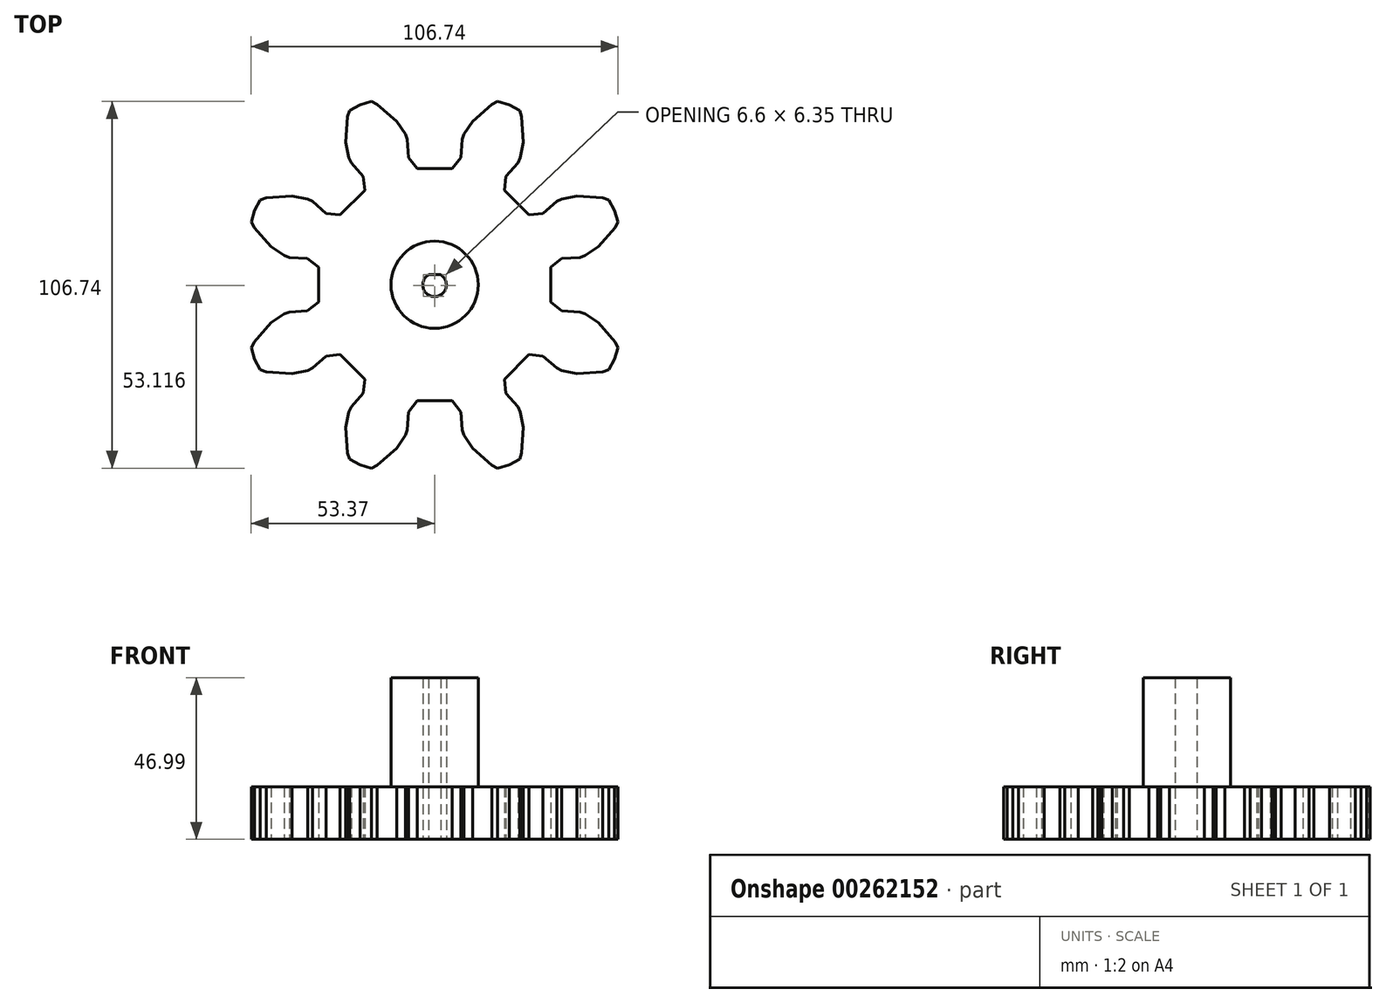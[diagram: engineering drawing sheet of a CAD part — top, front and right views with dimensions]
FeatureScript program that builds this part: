
annotation { "Feature Type Name" : "Feature", "Feature Type Description" : "" }
export const myFeature = defineFeature(function(context is Context, id is Id, definition is map)
    precondition{}
    {
        {
            var Q0;
            Q0=qCreatedBy(makeId("Top.planeOp"),FACE);
            var sketch = newSketch(context, id + "F0", { "sketchPlane" : qUnion([Q0])});
            skLineSegment(sketch, "E0", {"start": v(-50.73, 24.75) * mm, "end": v(-52.36, 21.69) * mm});
            skLineSegment(sketch, "E1", {"start": v(-52.36, 21.69) * mm, "end": v(-53.37, 18.37) * mm});
            skLineSegment(sketch, "E2", {"start": v(-53.37, 18.37) * mm, "end": v(-52.56, 16.72) * mm});
            skLineSegment(sketch, "E3", {"start": v(-52.56, 16.72) * mm, "end": v(-47.6, 11.05) * mm});
            skLineSegment(sketch, "E4", {"start": v(-47.6, 11.05) * mm, "end": v(-43.8, 8.5) * mm});
            skLineSegment(sketch, "E5", {"start": v(-43.8, 8.5) * mm, "end": v(-42.28, 7.97) * mm});
            skLineSegment(sketch, "E6", {"start": v(-42.28, 7.97) * mm, "end": v(-37.01, 7.62) * mm});
            skLineSegment(sketch, "E7", {"start": v(-37.01, 7.62) * mm, "end": v(-33.78, 5.07) * mm});
            skLineSegment(sketch, "E8", {"start": v(-33.78, 5.07) * mm, "end": v(-33.78, -5.07) * mm});
            skLineSegment(sketch, "E9", {"start": v(-33.78, -5.07) * mm, "end": v(-37.01, -7.62) * mm});
            skLineSegment(sketch, "E10", {"start": v(-37.01, -7.62) * mm, "end": v(-42.28, -7.97) * mm});
            skLineSegment(sketch, "E11", {"start": v(-42.28, -7.97) * mm, "end": v(-43.8, -8.5) * mm});
            skLineSegment(sketch, "E12", {"start": v(-43.8, -8.5) * mm, "end": v(-47.6, -11.05) * mm});
            skLineSegment(sketch, "E13", {"start": v(-47.6, -11.05) * mm, "end": v(-52.56, -16.72) * mm});
            skLineSegment(sketch, "E14", {"start": v(-52.56, -16.72) * mm, "end": v(-53.37, -18.37) * mm});
            skLineSegment(sketch, "E15", {"start": v(-53.37, -18.37) * mm, "end": v(-52.36, -21.69) * mm});
            skLineSegment(sketch, "E16", {"start": v(-52.36, -21.69) * mm, "end": v(-50.73, -24.75) * mm});
            skLineSegment(sketch, "E17", {"start": v(-50.73, -24.75) * mm, "end": v(-48.99, -25.34) * mm});
            skLineSegment(sketch, "E18", {"start": v(-48.99, -25.34) * mm, "end": v(-41.47, -25.85) * mm});
            skLineSegment(sketch, "E19", {"start": v(-41.47, -25.85) * mm, "end": v(-36.99, -24.97) * mm});
            skLineSegment(sketch, "E20", {"start": v(-36.99, -24.97) * mm, "end": v(-35.54, -24.26) * mm});
            skLineSegment(sketch, "E21", {"start": v(-35.54, -24.26) * mm, "end": v(-31.56, -20.79) * mm});
            skLineSegment(sketch, "E22", {"start": v(-31.56, -20.79) * mm, "end": v(-27.47, -20.3) * mm});
            skLineSegment(sketch, "E23", {"start": v(-27.47, -20.3) * mm, "end": v(-20.3, -27.47) * mm});
            skLineSegment(sketch, "E24", {"start": v(-20.3, -27.47) * mm, "end": v(-20.79, -31.56) * mm});
            skLineSegment(sketch, "E25", {"start": v(-20.79, -31.56) * mm, "end": v(-24.26, -35.54) * mm});
            skLineSegment(sketch, "E26", {"start": v(-24.26, -35.54) * mm, "end": v(-24.97, -36.99) * mm});
            skLineSegment(sketch, "E27", {"start": v(-24.97, -36.99) * mm, "end": v(-25.85, -41.47) * mm});
            skLineSegment(sketch, "E28", {"start": v(-25.85, -41.47) * mm, "end": v(-25.34, -48.99) * mm});
            skLineSegment(sketch, "E29", {"start": v(-25.34, -48.99) * mm, "end": v(-24.75, -50.73) * mm});
            skLineSegment(sketch, "E30", {"start": v(-24.75, -50.73) * mm, "end": v(-21.69, -52.36) * mm});
            skLineSegment(sketch, "E31", {"start": v(-21.69, -52.36) * mm, "end": v(-18.37, -53.37) * mm});
            skLineSegment(sketch, "E32", {"start": v(-18.37, -53.37) * mm, "end": v(-16.72, -52.56) * mm});
            skLineSegment(sketch, "E33", {"start": v(-16.72, -52.56) * mm, "end": v(-11.05, -47.6) * mm});
            skLineSegment(sketch, "E34", {"start": v(-11.05, -47.6) * mm, "end": v(-8.5, -43.8) * mm});
            skLineSegment(sketch, "E35", {"start": v(-8.5, -43.8) * mm, "end": v(-7.97, -42.28) * mm});
            skLineSegment(sketch, "E36", {"start": v(-7.97, -42.28) * mm, "end": v(-7.62, -37.01) * mm});
            skLineSegment(sketch, "E37", {"start": v(-7.62, -37.01) * mm, "end": v(-5.07, -33.78) * mm});
            skLineSegment(sketch, "E38", {"start": v(-5.07, -33.78) * mm, "end": v(5.07, -33.78) * mm});
            skLineSegment(sketch, "E39", {"start": v(5.07, -33.78) * mm, "end": v(7.62, -37.01) * mm});
            skLineSegment(sketch, "E40", {"start": v(7.62, -37.01) * mm, "end": v(7.97, -42.28) * mm});
            skLineSegment(sketch, "E41", {"start": v(7.97, -42.28) * mm, "end": v(8.5, -43.8) * mm});
            skLineSegment(sketch, "E42", {"start": v(8.5, -43.8) * mm, "end": v(11.05, -47.6) * mm});
            skLineSegment(sketch, "E43", {"start": v(11.05, -47.6) * mm, "end": v(16.72, -52.56) * mm});
            skLineSegment(sketch, "E44", {"start": v(16.72, -52.56) * mm, "end": v(18.37, -53.37) * mm});
            skLineSegment(sketch, "E45", {"start": v(18.37, -53.37) * mm, "end": v(21.69, -52.36) * mm});
            skLineSegment(sketch, "E46", {"start": v(21.69, -52.36) * mm, "end": v(24.75, -50.73) * mm});
            skLineSegment(sketch, "E47", {"start": v(24.75, -50.73) * mm, "end": v(25.34, -48.99) * mm});
            skLineSegment(sketch, "E48", {"start": v(25.34, -48.99) * mm, "end": v(25.85, -41.47) * mm});
            skLineSegment(sketch, "E49", {"start": v(25.85, -41.47) * mm, "end": v(24.97, -36.99) * mm});
            skLineSegment(sketch, "E50", {"start": v(24.97, -36.99) * mm, "end": v(24.26, -35.54) * mm});
            skLineSegment(sketch, "E51", {"start": v(24.26, -35.54) * mm, "end": v(20.79, -31.56) * mm});
            skLineSegment(sketch, "E52", {"start": v(20.79, -31.56) * mm, "end": v(20.3, -27.47) * mm});
            skLineSegment(sketch, "E53", {"start": v(20.3, -27.47) * mm, "end": v(27.47, -20.3) * mm});
            skLineSegment(sketch, "E54", {"start": v(27.47, -20.3) * mm, "end": v(31.56, -20.79) * mm});
            skLineSegment(sketch, "E55", {"start": v(31.56, -20.79) * mm, "end": v(35.54, -24.26) * mm});
            skLineSegment(sketch, "E56", {"start": v(35.54, -24.26) * mm, "end": v(36.99, -24.97) * mm});
            skLineSegment(sketch, "E57", {"start": v(36.99, -24.97) * mm, "end": v(41.47, -25.85) * mm});
            skLineSegment(sketch, "E58", {"start": v(41.47, -25.85) * mm, "end": v(48.99, -25.34) * mm});
            skLineSegment(sketch, "E59", {"start": v(48.99, -25.34) * mm, "end": v(50.73, -24.75) * mm});
            skLineSegment(sketch, "E60", {"start": v(50.73, -24.75) * mm, "end": v(52.36, -21.69) * mm});
            skLineSegment(sketch, "E61", {"start": v(52.36, -21.69) * mm, "end": v(53.37, -18.37) * mm});
            skLineSegment(sketch, "E62", {"start": v(53.37, -18.37) * mm, "end": v(52.56, -16.72) * mm});
            skLineSegment(sketch, "E63", {"start": v(52.56, -16.72) * mm, "end": v(47.6, -11.05) * mm});
            skLineSegment(sketch, "E64", {"start": v(47.6, -11.05) * mm, "end": v(43.8, -8.5) * mm});
            skLineSegment(sketch, "E65", {"start": v(43.8, -8.5) * mm, "end": v(42.28, -7.97) * mm});
            skLineSegment(sketch, "E66", {"start": v(42.28, -7.97) * mm, "end": v(37.01, -7.62) * mm});
            skLineSegment(sketch, "E67", {"start": v(37.01, -7.62) * mm, "end": v(33.78, -5.07) * mm});
            skLineSegment(sketch, "E68", {"start": v(33.78, -5.07) * mm, "end": v(33.78, 5.07) * mm});
            skLineSegment(sketch, "E69", {"start": v(33.78, 5.07) * mm, "end": v(37.01, 7.62) * mm});
            skLineSegment(sketch, "E70", {"start": v(37.01, 7.62) * mm, "end": v(42.28, 7.97) * mm});
            skLineSegment(sketch, "E71", {"start": v(42.28, 7.97) * mm, "end": v(43.8, 8.5) * mm});
            skLineSegment(sketch, "E72", {"start": v(43.8, 8.5) * mm, "end": v(47.6, 11.05) * mm});
            skLineSegment(sketch, "E73", {"start": v(47.6, 11.05) * mm, "end": v(52.56, 16.72) * mm});
            skLineSegment(sketch, "E74", {"start": v(52.56, 16.72) * mm, "end": v(53.37, 18.37) * mm});
            skLineSegment(sketch, "E75", {"start": v(53.37, 18.37) * mm, "end": v(52.36, 21.69) * mm});
            skLineSegment(sketch, "E76", {"start": v(52.36, 21.69) * mm, "end": v(50.73, 24.75) * mm});
            skLineSegment(sketch, "E77", {"start": v(50.73, 24.75) * mm, "end": v(48.99, 25.34) * mm});
            skLineSegment(sketch, "E78", {"start": v(48.99, 25.34) * mm, "end": v(41.47, 25.85) * mm});
            skLineSegment(sketch, "E79", {"start": v(41.47, 25.85) * mm, "end": v(36.99, 24.97) * mm});
            skLineSegment(sketch, "E80", {"start": v(36.99, 24.97) * mm, "end": v(35.54, 24.26) * mm});
            skLineSegment(sketch, "E81", {"start": v(35.54, 24.26) * mm, "end": v(31.56, 20.79) * mm});
            skLineSegment(sketch, "E82", {"start": v(31.56, 20.79) * mm, "end": v(27.47, 20.3) * mm});
            skLineSegment(sketch, "E83", {"start": v(27.47, 20.3) * mm, "end": v(20.3, 27.47) * mm});
            skLineSegment(sketch, "E84", {"start": v(20.3, 27.47) * mm, "end": v(20.79, 31.56) * mm});
            skLineSegment(sketch, "E85", {"start": v(20.79, 31.56) * mm, "end": v(24.26, 35.54) * mm});
            skLineSegment(sketch, "E86", {"start": v(24.26, 35.54) * mm, "end": v(24.97, 36.99) * mm});
            skLineSegment(sketch, "E87", {"start": v(24.97, 36.99) * mm, "end": v(25.85, 41.47) * mm});
            skLineSegment(sketch, "E88", {"start": v(25.85, 41.47) * mm, "end": v(25.34, 48.99) * mm});
            skLineSegment(sketch, "E89", {"start": v(25.34, 48.99) * mm, "end": v(24.75, 50.73) * mm});
            skLineSegment(sketch, "E90", {"start": v(24.75, 50.73) * mm, "end": v(21.69, 52.36) * mm});
            skLineSegment(sketch, "E91", {"start": v(21.69, 52.36) * mm, "end": v(18.37, 53.37) * mm});
            skLineSegment(sketch, "E92", {"start": v(18.37, 53.37) * mm, "end": v(16.72, 52.56) * mm});
            skLineSegment(sketch, "E93", {"start": v(16.72, 52.56) * mm, "end": v(11.05, 47.6) * mm});
            skLineSegment(sketch, "E94", {"start": v(11.05, 47.6) * mm, "end": v(8.5, 43.8) * mm});
            skLineSegment(sketch, "E95", {"start": v(8.5, 43.8) * mm, "end": v(7.97, 42.28) * mm});
            skLineSegment(sketch, "E96", {"start": v(7.97, 42.28) * mm, "end": v(7.62, 37.01) * mm});
            skLineSegment(sketch, "E97", {"start": v(7.62, 37.01) * mm, "end": v(5.07, 33.78) * mm});
            skLineSegment(sketch, "E98", {"start": v(5.07, 33.78) * mm, "end": v(-5.07, 33.78) * mm});
            skLineSegment(sketch, "E99", {"start": v(-5.07, 33.78) * mm, "end": v(-7.62, 37.01) * mm});
            skLineSegment(sketch, "E100", {"start": v(-7.62, 37.01) * mm, "end": v(-7.97, 42.28) * mm});
            skLineSegment(sketch, "E101", {"start": v(-7.97, 42.28) * mm, "end": v(-8.5, 43.8) * mm});
            skLineSegment(sketch, "E102", {"start": v(-8.5, 43.8) * mm, "end": v(-11.05, 47.6) * mm});
            skLineSegment(sketch, "E103", {"start": v(-11.05, 47.6) * mm, "end": v(-16.72, 52.56) * mm});
            skLineSegment(sketch, "E104", {"start": v(-16.72, 52.56) * mm, "end": v(-18.37, 53.37) * mm});
            skLineSegment(sketch, "E105", {"start": v(-18.37, 53.37) * mm, "end": v(-21.69, 52.36) * mm});
            skLineSegment(sketch, "E106", {"start": v(-21.69, 52.36) * mm, "end": v(-24.75, 50.73) * mm});
            skLineSegment(sketch, "E107", {"start": v(-24.75, 50.73) * mm, "end": v(-25.34, 48.99) * mm});
            skLineSegment(sketch, "E108", {"start": v(-25.34, 48.99) * mm, "end": v(-25.85, 41.47) * mm});
            skLineSegment(sketch, "E109", {"start": v(-25.85, 41.47) * mm, "end": v(-24.97, 36.99) * mm});
            skLineSegment(sketch, "E110", {"start": v(-24.97, 36.99) * mm, "end": v(-24.26, 35.54) * mm});
            skLineSegment(sketch, "E111", {"start": v(-24.26, 35.54) * mm, "end": v(-20.79, 31.56) * mm});
            skLineSegment(sketch, "E112", {"start": v(-20.79, 31.56) * mm, "end": v(-20.3, 27.47) * mm});
            skLineSegment(sketch, "E113", {"start": v(-20.3, 27.47) * mm, "end": v(-27.47, 20.3) * mm});
            skLineSegment(sketch, "E114", {"start": v(-27.47, 20.3) * mm, "end": v(-31.56, 20.79) * mm});
            skLineSegment(sketch, "E115", {"start": v(-31.56, 20.79) * mm, "end": v(-35.54, 24.26) * mm});
            skLineSegment(sketch, "E116", {"start": v(-35.54, 24.26) * mm, "end": v(-36.99, 24.97) * mm});
            skLineSegment(sketch, "E117", {"start": v(-36.99, 24.97) * mm, "end": v(-41.47, 25.85) * mm});
            skLineSegment(sketch, "E118", {"start": v(-41.47, 25.85) * mm, "end": v(-48.99, 25.34) * mm});
            skLineSegment(sketch, "E119", {"start": v(-48.99, 25.34) * mm, "end": v(-50.73, 24.75) * mm});
            skLineSegment(sketch, "E120", {"start": v(-5.04, 7.34) * mm, "end": v(-3.4, 8.22) * mm});
            skLineSegment(sketch, "E121", {"start": v(-3.4, 8.22) * mm, "end": v(-1.62, 8.75) * mm});
            skLineSegment(sketch, "E122", {"start": v(-1.62, 8.75) * mm, "end": v(0.23, 8.9) * mm});
            skLineSegment(sketch, "E123", {"start": v(0.23, 8.9) * mm, "end": v(2.08, 8.66) * mm});
            skLineSegment(sketch, "E124", {"start": v(2.08, 8.66) * mm, "end": v(3.83, 8.04) * mm});
            skLineSegment(sketch, "E125", {"start": v(3.83, 8.04) * mm, "end": v(5.42, 7.06) * mm});
            skLineSegment(sketch, "E126", {"start": v(5.42, 7.06) * mm, "end": v(6.77, 5.78) * mm});
            skLineSegment(sketch, "E127", {"start": v(6.77, 5.78) * mm, "end": v(7.82, 4.25) * mm});
            skLineSegment(sketch, "E128", {"start": v(7.82, 4.25) * mm, "end": v(8.54, 2.53) * mm});
            skLineSegment(sketch, "E129", {"start": v(8.54, 2.53) * mm, "end": v(8.87, 0.7) * mm});
            skLineSegment(sketch, "E130", {"start": v(8.87, 0.7) * mm, "end": v(8.83, -1.16) * mm});
            skLineSegment(sketch, "E131", {"start": v(8.83, -1.16) * mm, "end": v(8.4, -2.97) * mm});
            skLineSegment(sketch, "E132", {"start": v(8.4, -2.97) * mm, "end": v(7.6, -4.65) * mm});
            skLineSegment(sketch, "E133", {"start": v(7.6, -4.65) * mm, "end": v(6.46, -6.13) * mm});
            skLineSegment(sketch, "E134", {"start": v(6.46, -6.13) * mm, "end": v(5.04, -7.34) * mm});
            skLineSegment(sketch, "E135", {"start": v(5.04, -7.34) * mm, "end": v(3.4, -8.22) * mm});
            skLineSegment(sketch, "E136", {"start": v(3.4, -8.22) * mm, "end": v(1.62, -8.75) * mm});
            skLineSegment(sketch, "E137", {"start": v(1.62, -8.75) * mm, "end": v(-0.23, -8.9) * mm});
            skLineSegment(sketch, "E138", {"start": v(-0.23, -8.9) * mm, "end": v(-2.08, -8.66) * mm});
            skLineSegment(sketch, "E139", {"start": v(-2.08, -8.66) * mm, "end": v(-3.83, -8.04) * mm});
            skLineSegment(sketch, "E140", {"start": v(-3.83, -8.04) * mm, "end": v(-5.42, -7.06) * mm});
            skLineSegment(sketch, "E141", {"start": v(-5.42, -7.06) * mm, "end": v(-6.77, -5.78) * mm});
            skLineSegment(sketch, "E142", {"start": v(-6.77, -5.78) * mm, "end": v(-7.82, -4.25) * mm});
            skLineSegment(sketch, "E143", {"start": v(-7.82, -4.25) * mm, "end": v(-8.54, -2.53) * mm});
            skLineSegment(sketch, "E144", {"start": v(-8.54, -2.53) * mm, "end": v(-8.87, -0.7) * mm});
            skLineSegment(sketch, "E145", {"start": v(-8.87, -0.7) * mm, "end": v(-8.83, 1.16) * mm});
            skLineSegment(sketch, "E146", {"start": v(-8.83, 1.16) * mm, "end": v(-8.4, 2.97) * mm});
            skLineSegment(sketch, "E147", {"start": v(-8.4, 2.97) * mm, "end": v(-7.6, 4.65) * mm});
            skLineSegment(sketch, "E148", {"start": v(-7.6, 4.65) * mm, "end": v(-6.46, 6.13) * mm});
            skLineSegment(sketch, "E149", {"start": v(-6.46, 6.13) * mm, "end": v(-5.04, 7.34) * mm});
            skSolve(sketch);
        }
        {
            var Q0;
            Q0=makeQuery(id+"F0.imprint","IMPRINT",FACE,{"disambiguationData":[TD([[makeQuery(id+"F0.imprint","IMPRINT",EDGE,{"derivedFrom":sQuery(id+"F0.wireOp",EDGE,"E0")}),1.0]])]});
            var Q1;
            Q1=makeQuery(id+"F0.imprint","IMPRINT",FACE,{"disambiguationData":[TD([[makeQuery(id+"F0.imprint","IMPRINT",EDGE,{"derivedFrom":sQuery(id+"F0.wireOp",EDGE,"E120")}),-1.0]])]});
            extrude(context, id + "F1", {"entities" : qUnion([Q0, Q1]), "depth" : 15.24 * mm});
        }
        {
            var Q0;
            Q0=makeQuery(id+"F1.opExtrude","CAP_FACE",FACE,{"disambiguationData":[OSD([sQuery(id+"F0.wireOp",EDGE,"E0"),sQuery(id+"F0.wireOp",EDGE,"E1"),sQuery(id+"F0.wireOp",EDGE,"E2"),sQuery(id+"F0.wireOp",EDGE,"E3"),sQuery(id+"F0.wireOp",EDGE,"E4"),sQuery(id+"F0.wireOp",EDGE,"E5"),sQuery(id+"F0.wireOp",EDGE,"E6"),sQuery(id+"F0.wireOp",EDGE,"E7"),sQuery(id+"F0.wireOp",EDGE,"E8"),sQuery(id+"F0.wireOp",EDGE,"E9"),sQuery(id+"F0.wireOp",EDGE,"E10"),sQuery(id+"F0.wireOp",EDGE,"E11"),sQuery(id+"F0.wireOp",EDGE,"E12"),sQuery(id+"F0.wireOp",EDGE,"E13"),sQuery(id+"F0.wireOp",EDGE,"E14"),sQuery(id+"F0.wireOp",EDGE,"E15"),sQuery(id+"F0.wireOp",EDGE,"E16"),sQuery(id+"F0.wireOp",EDGE,"E17"),sQuery(id+"F0.wireOp",EDGE,"E18"),sQuery(id+"F0.wireOp",EDGE,"E19"),sQuery(id+"F0.wireOp",EDGE,"E20"),sQuery(id+"F0.wireOp",EDGE,"E21"),sQuery(id+"F0.wireOp",EDGE,"E22"),sQuery(id+"F0.wireOp",EDGE,"E23"),sQuery(id+"F0.wireOp",EDGE,"E24"),sQuery(id+"F0.wireOp",EDGE,"E25"),sQuery(id+"F0.wireOp",EDGE,"E26"),sQuery(id+"F0.wireOp",EDGE,"E27"),sQuery(id+"F0.wireOp",EDGE,"E28"),sQuery(id+"F0.wireOp",EDGE,"E29"),sQuery(id+"F0.wireOp",EDGE,"E30"),sQuery(id+"F0.wireOp",EDGE,"E31"),sQuery(id+"F0.wireOp",EDGE,"E32"),sQuery(id+"F0.wireOp",EDGE,"E33"),sQuery(id+"F0.wireOp",EDGE,"E34"),sQuery(id+"F0.wireOp",EDGE,"E35"),sQuery(id+"F0.wireOp",EDGE,"E36"),sQuery(id+"F0.wireOp",EDGE,"E37"),sQuery(id+"F0.wireOp",EDGE,"E38"),sQuery(id+"F0.wireOp",EDGE,"E39"),sQuery(id+"F0.wireOp",EDGE,"E40"),sQuery(id+"F0.wireOp",EDGE,"E41"),sQuery(id+"F0.wireOp",EDGE,"E42"),sQuery(id+"F0.wireOp",EDGE,"E43"),sQuery(id+"F0.wireOp",EDGE,"E44"),sQuery(id+"F0.wireOp",EDGE,"E45"),sQuery(id+"F0.wireOp",EDGE,"E46"),sQuery(id+"F0.wireOp",EDGE,"E47"),sQuery(id+"F0.wireOp",EDGE,"E48"),sQuery(id+"F0.wireOp",EDGE,"E49"),sQuery(id+"F0.wireOp",EDGE,"E50"),sQuery(id+"F0.wireOp",EDGE,"E51"),sQuery(id+"F0.wireOp",EDGE,"E52"),sQuery(id+"F0.wireOp",EDGE,"E53"),sQuery(id+"F0.wireOp",EDGE,"E54"),sQuery(id+"F0.wireOp",EDGE,"E55"),sQuery(id+"F0.wireOp",EDGE,"E56"),sQuery(id+"F0.wireOp",EDGE,"E57"),sQuery(id+"F0.wireOp",EDGE,"E58"),sQuery(id+"F0.wireOp",EDGE,"E59"),sQuery(id+"F0.wireOp",EDGE,"E60"),sQuery(id+"F0.wireOp",EDGE,"E61"),sQuery(id+"F0.wireOp",EDGE,"E62"),sQuery(id+"F0.wireOp",EDGE,"E63"),sQuery(id+"F0.wireOp",EDGE,"E64"),sQuery(id+"F0.wireOp",EDGE,"E65"),sQuery(id+"F0.wireOp",EDGE,"E66"),sQuery(id+"F0.wireOp",EDGE,"E67"),sQuery(id+"F0.wireOp",EDGE,"E68"),sQuery(id+"F0.wireOp",EDGE,"E69"),sQuery(id+"F0.wireOp",EDGE,"E70"),sQuery(id+"F0.wireOp",EDGE,"E71"),sQuery(id+"F0.wireOp",EDGE,"E72"),sQuery(id+"F0.wireOp",EDGE,"E73"),sQuery(id+"F0.wireOp",EDGE,"E74"),sQuery(id+"F0.wireOp",EDGE,"E75"),sQuery(id+"F0.wireOp",EDGE,"E76"),sQuery(id+"F0.wireOp",EDGE,"E77"),sQuery(id+"F0.wireOp",EDGE,"E78"),sQuery(id+"F0.wireOp",EDGE,"E79"),sQuery(id+"F0.wireOp",EDGE,"E80"),sQuery(id+"F0.wireOp",EDGE,"E81"),sQuery(id+"F0.wireOp",EDGE,"E82"),sQuery(id+"F0.wireOp",EDGE,"E83"),sQuery(id+"F0.wireOp",EDGE,"E84"),sQuery(id+"F0.wireOp",EDGE,"E85"),sQuery(id+"F0.wireOp",EDGE,"E86"),sQuery(id+"F0.wireOp",EDGE,"E87"),sQuery(id+"F0.wireOp",EDGE,"E88"),sQuery(id+"F0.wireOp",EDGE,"E89"),sQuery(id+"F0.wireOp",EDGE,"E90"),sQuery(id+"F0.wireOp",EDGE,"E91"),sQuery(id+"F0.wireOp",EDGE,"E92"),sQuery(id+"F0.wireOp",EDGE,"E93"),sQuery(id+"F0.wireOp",EDGE,"E94"),sQuery(id+"F0.wireOp",EDGE,"E95"),sQuery(id+"F0.wireOp",EDGE,"E96"),sQuery(id+"F0.wireOp",EDGE,"E97"),sQuery(id+"F0.wireOp",EDGE,"E98"),sQuery(id+"F0.wireOp",EDGE,"E99"),sQuery(id+"F0.wireOp",EDGE,"E100"),sQuery(id+"F0.wireOp",EDGE,"E101"),sQuery(id+"F0.wireOp",EDGE,"E102"),sQuery(id+"F0.wireOp",EDGE,"E103"),sQuery(id+"F0.wireOp",EDGE,"E104"),sQuery(id+"F0.wireOp",EDGE,"E105"),sQuery(id+"F0.wireOp",EDGE,"E106"),sQuery(id+"F0.wireOp",EDGE,"E107"),sQuery(id+"F0.wireOp",EDGE,"E108"),sQuery(id+"F0.wireOp",EDGE,"E109"),sQuery(id+"F0.wireOp",EDGE,"E110"),sQuery(id+"F0.wireOp",EDGE,"E111"),sQuery(id+"F0.wireOp",EDGE,"E112"),sQuery(id+"F0.wireOp",EDGE,"E113"),sQuery(id+"F0.wireOp",EDGE,"E114"),sQuery(id+"F0.wireOp",EDGE,"E115"),sQuery(id+"F0.wireOp",EDGE,"E116"),sQuery(id+"F0.wireOp",EDGE,"E117"),sQuery(id+"F0.wireOp",EDGE,"E118"),sQuery(id+"F0.wireOp",EDGE,"E119")])],"isStart":false});
            var sketch = newSketch(context, id + "F2", { "sketchPlane" : qUnion([Q0])});
            skCircle(sketch, "E150", {"center": v(0, 0) * mm, "radius": 3.43 * mm});
            skLineSegment(sketch, "E151", {"start": v(4.59, 2.92) * mm, "end": v(-4.97, 2.92) * mm});
            skCircle(sketch, "E152", {"center": v(0, 0) * mm, "radius": 12.7 * mm});
            skCircle(sketch, "E153", {"center": v(0, 0) * mm, "radius": 19.05 * mm});
            skSolve(sketch);
        }
        {
            var Q0;
            Q0=makeQuery(id+"F2.imprint","IMPRINT",FACE,{"disambiguationData":[TD([[makeQuery(id+"F2.imprint","IMPRINT",EDGE,{"derivedFrom":sQuery(id+"F2.wireOp",EDGE,"E152")}),1.0]])]});
            var Q1;
            {var subQ0=sQuery(id+"F2.wireOp",EDGE,"E151");var subQ1=sQuery(id+"F2.wireOp",EDGE,"E150");var subQ2=makeQuery(id+"F2.imprint","INTERSECT",VERTEX,{"disambiguationData":[OD(0.0)],"derivedFrom":[subQ1,subQ0]});Q1=makeQuery(id+"F2.imprint","IMPRINT",FACE,{"disambiguationData":[TD([[makeQuery(id+"F2.imprint","IMPRINT",EDGE,{"disambiguationData":[TD([[subQ2,1.0]])],"derivedFrom":subQ1}),1.0]])]});}
            extrude(context, id + "F3", {"entities" : qUnion([Q0, Q1]), "operationType" : NewBodyOperationType.ADD, "depth" : 31.75 * mm});
        }
        {
            var Q0;
            Q0=makeQuery(id+"F3.boolean.opBoolean","SPLIT",FACE,{"disambiguationData":[TD([makeQuery(id+"F3.opExtrude","SWEPT_FACE",FACE,{"disambiguationData":[OSD([sQuery(id+"F2.wireOp",EDGE,"E150")])]})])],"derivedFrom":makeQuery(id+"F1.opExtrude","CAP_FACE",FACE,{"disambiguationData":[OSD([sQuery(id+"F0.wireOp",EDGE,"E0"),sQuery(id+"F0.wireOp",EDGE,"E1"),sQuery(id+"F0.wireOp",EDGE,"E2"),sQuery(id+"F0.wireOp",EDGE,"E3"),sQuery(id+"F0.wireOp",EDGE,"E4"),sQuery(id+"F0.wireOp",EDGE,"E5"),sQuery(id+"F0.wireOp",EDGE,"E6"),sQuery(id+"F0.wireOp",EDGE,"E7"),sQuery(id+"F0.wireOp",EDGE,"E8"),sQuery(id+"F0.wireOp",EDGE,"E9"),sQuery(id+"F0.wireOp",EDGE,"E10"),sQuery(id+"F0.wireOp",EDGE,"E11"),sQuery(id+"F0.wireOp",EDGE,"E12"),sQuery(id+"F0.wireOp",EDGE,"E13"),sQuery(id+"F0.wireOp",EDGE,"E14"),sQuery(id+"F0.wireOp",EDGE,"E15"),sQuery(id+"F0.wireOp",EDGE,"E16"),sQuery(id+"F0.wireOp",EDGE,"E17"),sQuery(id+"F0.wireOp",EDGE,"E18"),sQuery(id+"F0.wireOp",EDGE,"E19"),sQuery(id+"F0.wireOp",EDGE,"E20"),sQuery(id+"F0.wireOp",EDGE,"E21"),sQuery(id+"F0.wireOp",EDGE,"E22"),sQuery(id+"F0.wireOp",EDGE,"E23"),sQuery(id+"F0.wireOp",EDGE,"E24"),sQuery(id+"F0.wireOp",EDGE,"E25"),sQuery(id+"F0.wireOp",EDGE,"E26"),sQuery(id+"F0.wireOp",EDGE,"E27"),sQuery(id+"F0.wireOp",EDGE,"E28"),sQuery(id+"F0.wireOp",EDGE,"E29"),sQuery(id+"F0.wireOp",EDGE,"E30"),sQuery(id+"F0.wireOp",EDGE,"E31"),sQuery(id+"F0.wireOp",EDGE,"E32"),sQuery(id+"F0.wireOp",EDGE,"E33"),sQuery(id+"F0.wireOp",EDGE,"E34"),sQuery(id+"F0.wireOp",EDGE,"E35"),sQuery(id+"F0.wireOp",EDGE,"E36"),sQuery(id+"F0.wireOp",EDGE,"E37"),sQuery(id+"F0.wireOp",EDGE,"E38"),sQuery(id+"F0.wireOp",EDGE,"E39"),sQuery(id+"F0.wireOp",EDGE,"E40"),sQuery(id+"F0.wireOp",EDGE,"E41"),sQuery(id+"F0.wireOp",EDGE,"E42"),sQuery(id+"F0.wireOp",EDGE,"E43"),sQuery(id+"F0.wireOp",EDGE,"E44"),sQuery(id+"F0.wireOp",EDGE,"E45"),sQuery(id+"F0.wireOp",EDGE,"E46"),sQuery(id+"F0.wireOp",EDGE,"E47"),sQuery(id+"F0.wireOp",EDGE,"E48"),sQuery(id+"F0.wireOp",EDGE,"E49"),sQuery(id+"F0.wireOp",EDGE,"E50"),sQuery(id+"F0.wireOp",EDGE,"E51"),sQuery(id+"F0.wireOp",EDGE,"E52"),sQuery(id+"F0.wireOp",EDGE,"E53"),sQuery(id+"F0.wireOp",EDGE,"E54"),sQuery(id+"F0.wireOp",EDGE,"E55"),sQuery(id+"F0.wireOp",EDGE,"E56"),sQuery(id+"F0.wireOp",EDGE,"E57"),sQuery(id+"F0.wireOp",EDGE,"E58"),sQuery(id+"F0.wireOp",EDGE,"E59"),sQuery(id+"F0.wireOp",EDGE,"E60"),sQuery(id+"F0.wireOp",EDGE,"E61"),sQuery(id+"F0.wireOp",EDGE,"E62"),sQuery(id+"F0.wireOp",EDGE,"E63"),sQuery(id+"F0.wireOp",EDGE,"E64"),sQuery(id+"F0.wireOp",EDGE,"E65"),sQuery(id+"F0.wireOp",EDGE,"E66"),sQuery(id+"F0.wireOp",EDGE,"E67"),sQuery(id+"F0.wireOp",EDGE,"E68"),sQuery(id+"F0.wireOp",EDGE,"E69"),sQuery(id+"F0.wireOp",EDGE,"E70"),sQuery(id+"F0.wireOp",EDGE,"E71"),sQuery(id+"F0.wireOp",EDGE,"E72"),sQuery(id+"F0.wireOp",EDGE,"E73"),sQuery(id+"F0.wireOp",EDGE,"E74"),sQuery(id+"F0.wireOp",EDGE,"E75"),sQuery(id+"F0.wireOp",EDGE,"E76"),sQuery(id+"F0.wireOp",EDGE,"E77"),sQuery(id+"F0.wireOp",EDGE,"E78"),sQuery(id+"F0.wireOp",EDGE,"E79"),sQuery(id+"F0.wireOp",EDGE,"E80"),sQuery(id+"F0.wireOp",EDGE,"E81"),sQuery(id+"F0.wireOp",EDGE,"E82"),sQuery(id+"F0.wireOp",EDGE,"E83"),sQuery(id+"F0.wireOp",EDGE,"E84"),sQuery(id+"F0.wireOp",EDGE,"E85"),sQuery(id+"F0.wireOp",EDGE,"E86"),sQuery(id+"F0.wireOp",EDGE,"E87"),sQuery(id+"F0.wireOp",EDGE,"E88"),sQuery(id+"F0.wireOp",EDGE,"E89"),sQuery(id+"F0.wireOp",EDGE,"E90"),sQuery(id+"F0.wireOp",EDGE,"E91"),sQuery(id+"F0.wireOp",EDGE,"E92"),sQuery(id+"F0.wireOp",EDGE,"E93"),sQuery(id+"F0.wireOp",EDGE,"E94"),sQuery(id+"F0.wireOp",EDGE,"E95"),sQuery(id+"F0.wireOp",EDGE,"E96"),sQuery(id+"F0.wireOp",EDGE,"E97"),sQuery(id+"F0.wireOp",EDGE,"E98"),sQuery(id+"F0.wireOp",EDGE,"E99"),sQuery(id+"F0.wireOp",EDGE,"E100"),sQuery(id+"F0.wireOp",EDGE,"E101"),sQuery(id+"F0.wireOp",EDGE,"E102"),sQuery(id+"F0.wireOp",EDGE,"E103"),sQuery(id+"F0.wireOp",EDGE,"E104"),sQuery(id+"F0.wireOp",EDGE,"E105"),sQuery(id+"F0.wireOp",EDGE,"E106"),sQuery(id+"F0.wireOp",EDGE,"E107"),sQuery(id+"F0.wireOp",EDGE,"E108"),sQuery(id+"F0.wireOp",EDGE,"E109"),sQuery(id+"F0.wireOp",EDGE,"E110"),sQuery(id+"F0.wireOp",EDGE,"E111"),sQuery(id+"F0.wireOp",EDGE,"E112"),sQuery(id+"F0.wireOp",EDGE,"E113"),sQuery(id+"F0.wireOp",EDGE,"E114"),sQuery(id+"F0.wireOp",EDGE,"E115"),sQuery(id+"F0.wireOp",EDGE,"E116"),sQuery(id+"F0.wireOp",EDGE,"E117"),sQuery(id+"F0.wireOp",EDGE,"E118"),sQuery(id+"F0.wireOp",EDGE,"E119")])],"isStart":false})});
            extrude(context, id + "F4", {"entities" : qUnion([Q0]), "operationType" : NewBodyOperationType.REMOVE, "oppositeDirection" : true, "depth" : 25.4 * mm});
        }
    });
